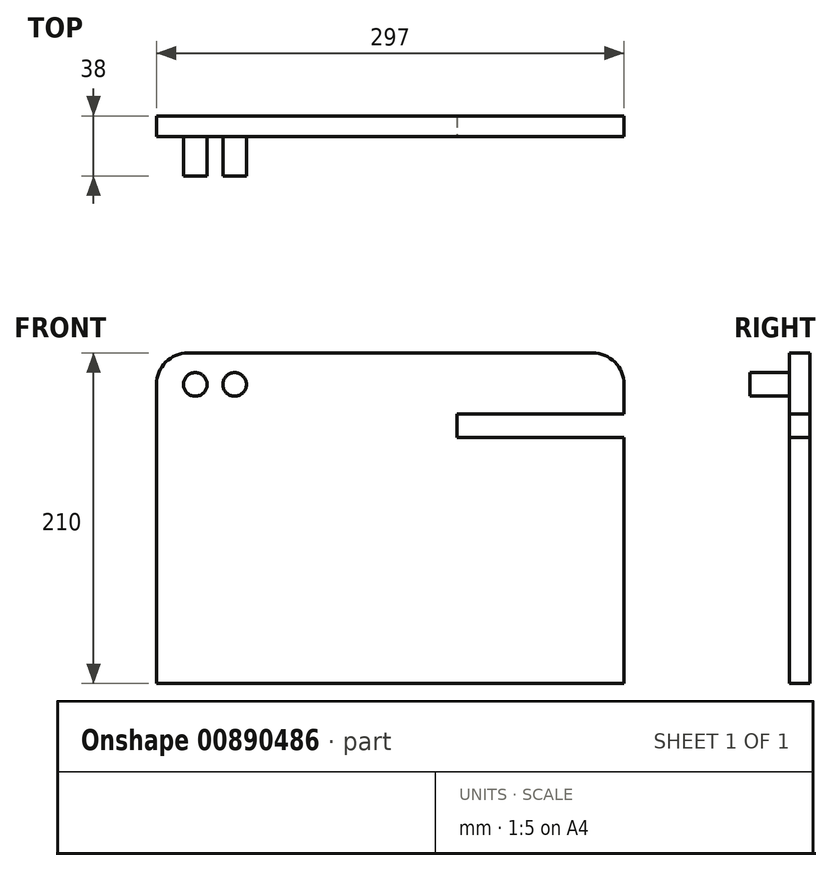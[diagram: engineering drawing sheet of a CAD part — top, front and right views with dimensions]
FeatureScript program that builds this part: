
annotation { "Feature Type Name" : "Feature", "Feature Type Description" : "" }
export const myFeature = defineFeature(function(context is Context, id is Id, definition is map)
    precondition{}
    {
        {
            var Q0;
            Q0=qCreatedBy(makeId("Front.planeOp"),FACE);
            var sketch = newSketch(context, id + "F0", { "sketchPlane" : qUnion([Q0])});
            skLineSegment(sketch, "E0.bottom", {"start": v(-120.67, 118.96) * mm, "end": v(136.33, 118.96) * mm});
            skLineSegment(sketch, "E0.top", {"start": v(-140.67, -91.04) * mm, "end": v(156.33, -91.04) * mm});
            skLineSegment(sketch, "E0.left", {"start": v(-140.67, 98.96) * mm, "end": v(-140.67, -91.04) * mm});
            skLineSegment(sketch, "E0.right", {"start": v(156.33, 98.96) * mm, "end": v(156.33, -91.04) * mm});
            skPoint(sketch, "E1.visualSharp", {"position": v(-140.67, 118.96) * mm});
            skArc(sketch, "E1.filletArc", {"start": v(-120.67, 118.96) * mm, "mid": v(-134.81, 113.1) * mm, "end": v(-140.67, 98.96) * mm});
            skPoint(sketch, "E2.visualSharp", {"position": v(156.33, 118.96) * mm});
            skArc(sketch, "E2.filletArc", {"start": v(156.33, 98.96) * mm, "mid": v(150.47, 113.1) * mm, "end": v(136.33, 118.96) * mm});
            skSolve(sketch);
        }
        {
            var Q0;
            Q0 = qSketchRegion(id + "F0", true);
            extrude(context, id + "F1", {"entities" : qUnion([Q0]), "depth" : 13 * mm, "offsetDistance" : 25 * mm});
        }
        {
            var Q0;
            Q0=makeQuery(id+"F1.opExtrude","CAP_FACE",FACE,{"disambiguationData":[OSD([sQuery(id+"F0.wireOp",EDGE,"E0.bottom"),sQuery(id+"F0.wireOp",EDGE,"E0.top"),sQuery(id+"F0.wireOp",EDGE,"E0.left"),sQuery(id+"F0.wireOp",EDGE,"E0.right"),sQuery(id+"F0.wireOp",EDGE,"E1.filletArc"),sQuery(id+"F0.wireOp",EDGE,"E2.filletArc")])],"isStart":false});
            var sketch = newSketch(context, id + "F2", { "sketchPlane" : qUnion([Q0])});
            skLineSegment(sketch, "E3.bottom", {"start": v(160.15, 80.16) * mm, "end": v(50.15, 80.16) * mm});
            skLineSegment(sketch, "E3.top", {"start": v(160.15, 65.16) * mm, "end": v(50.15, 65.16) * mm});
            skLineSegment(sketch, "E3.left", {"start": v(160.15, 80.16) * mm, "end": v(160.15, 65.16) * mm});
            skLineSegment(sketch, "E3.right", {"start": v(50.15, 80.16) * mm, "end": v(50.15, 65.16) * mm});
            skSolve(sketch);
        }
        {
            var Q0;
            Q0 = qSketchRegion(id + "F2", true);
            extrude(context, id + "F3", {"entities" : qUnion([Q0]), "operationType" : NewBodyOperationType.REMOVE, "oppositeDirection" : true, "depth" : 25 * mm, "offsetDistance" : 25 * mm});
        }
        {
            var Q0;
            Q0=makeQuery(id+"F1.opExtrude","CAP_FACE",FACE,{"disambiguationData":[OSD([sQuery(id+"F0.wireOp",EDGE,"E0.bottom"),sQuery(id+"F0.wireOp",EDGE,"E0.top"),sQuery(id+"F0.wireOp",EDGE,"E0.left"),sQuery(id+"F0.wireOp",EDGE,"E0.right"),sQuery(id+"F0.wireOp",EDGE,"E1.filletArc"),sQuery(id+"F0.wireOp",EDGE,"E2.filletArc")])],"isStart":false});
            var sketch = newSketch(context, id + "F4", { "sketchPlane" : qUnion([Q0])});
            skCircle(sketch, "E4", {"center": v(-116.05, 98.96) * mm, "radius": 7.5 * mm});
            skCircle(sketch, "E5", {"center": v(-91.05, 98.96) * mm, "radius": 7.5 * mm});
            skSolve(sketch);
        }
        {
            var Q0;
            Q0=makeQuery(id+"F4.imprint","IMPRINT",FACE,{"disambiguationData":[TD([[makeQuery(id+"F4.imprint","IMPRINT",EDGE,{"derivedFrom":sQuery(id+"F4.wireOp",EDGE,"E4")}),1.0]])]});
            var Q1;
            Q1=makeQuery(id+"F4.imprint","IMPRINT",FACE,{"disambiguationData":[TD([[makeQuery(id+"F4.imprint","IMPRINT",EDGE,{"derivedFrom":sQuery(id+"F4.wireOp",EDGE,"E5")}),1.0]])]});
            extrude(context, id + "F5", {"entities" : qUnion([Q0, Q1]), "operationType" : NewBodyOperationType.ADD, "depth" : 25 * mm, "offsetDistance" : 25 * mm});
        }
    });
